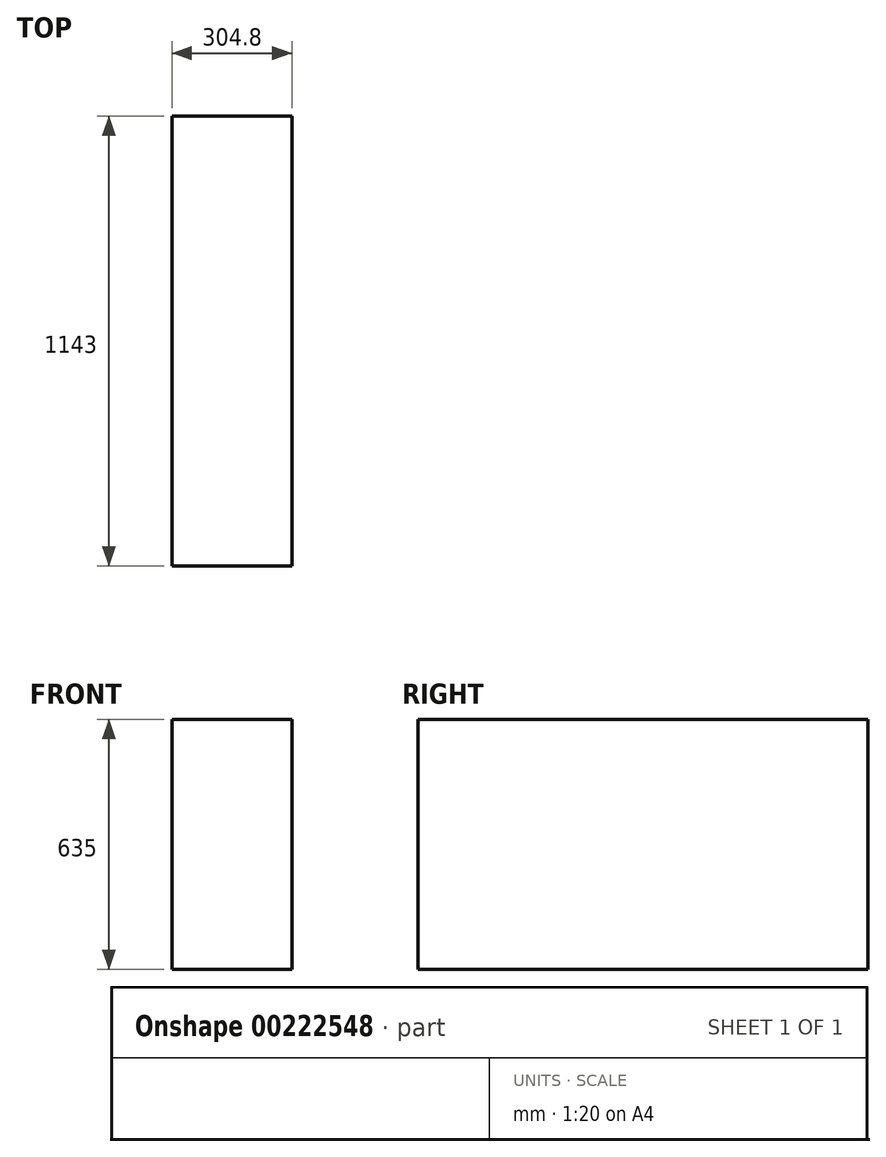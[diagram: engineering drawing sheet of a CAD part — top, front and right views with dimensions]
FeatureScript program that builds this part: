
annotation { "Feature Type Name" : "Feature", "Feature Type Description" : "" }
export const myFeature = defineFeature(function(context is Context, id is Id, definition is map)
    precondition{}
    {
        {
            var Q0;
            Q0=qCreatedBy(makeId("Right.planeOp"),FACE);
            var sketch = newSketch(context, id + "F0", { "sketchPlane" : qUnion([Q0])});
            skLineSegment(sketch, "E0.bottom", {"start": v(-571.5, 63.5) * mm, "end": v(571.5, 63.5) * mm});
            skLineSegment(sketch, "E0.top", {"start": v(-571.5, -571.5) * mm, "end": v(571.5, -571.5) * mm});
            skLineSegment(sketch, "E0.left", {"start": v(-571.5, 63.5) * mm, "end": v(-571.5, -571.5) * mm});
            skLineSegment(sketch, "E0.right", {"start": v(571.5, 63.5) * mm, "end": v(571.5, -571.5) * mm});
            skSolve(sketch);
        }
        {
            var Q0;
            Q0=makeQuery(id+"F0.imprint","IMPRINT",FACE,{"disambiguationData":[TD([[makeQuery(id+"F0.imprint","IMPRINT",EDGE,{"derivedFrom":sQuery(id+"F0.wireOp",EDGE,"E0.bottom")}),-1.0]])]});
            extrude(context, id + "F1", {"entities" : qUnion([Q0]), "endBound" : BoundingType.SYMMETRIC, "depth" : 304.8 * mm});
        }
    });
